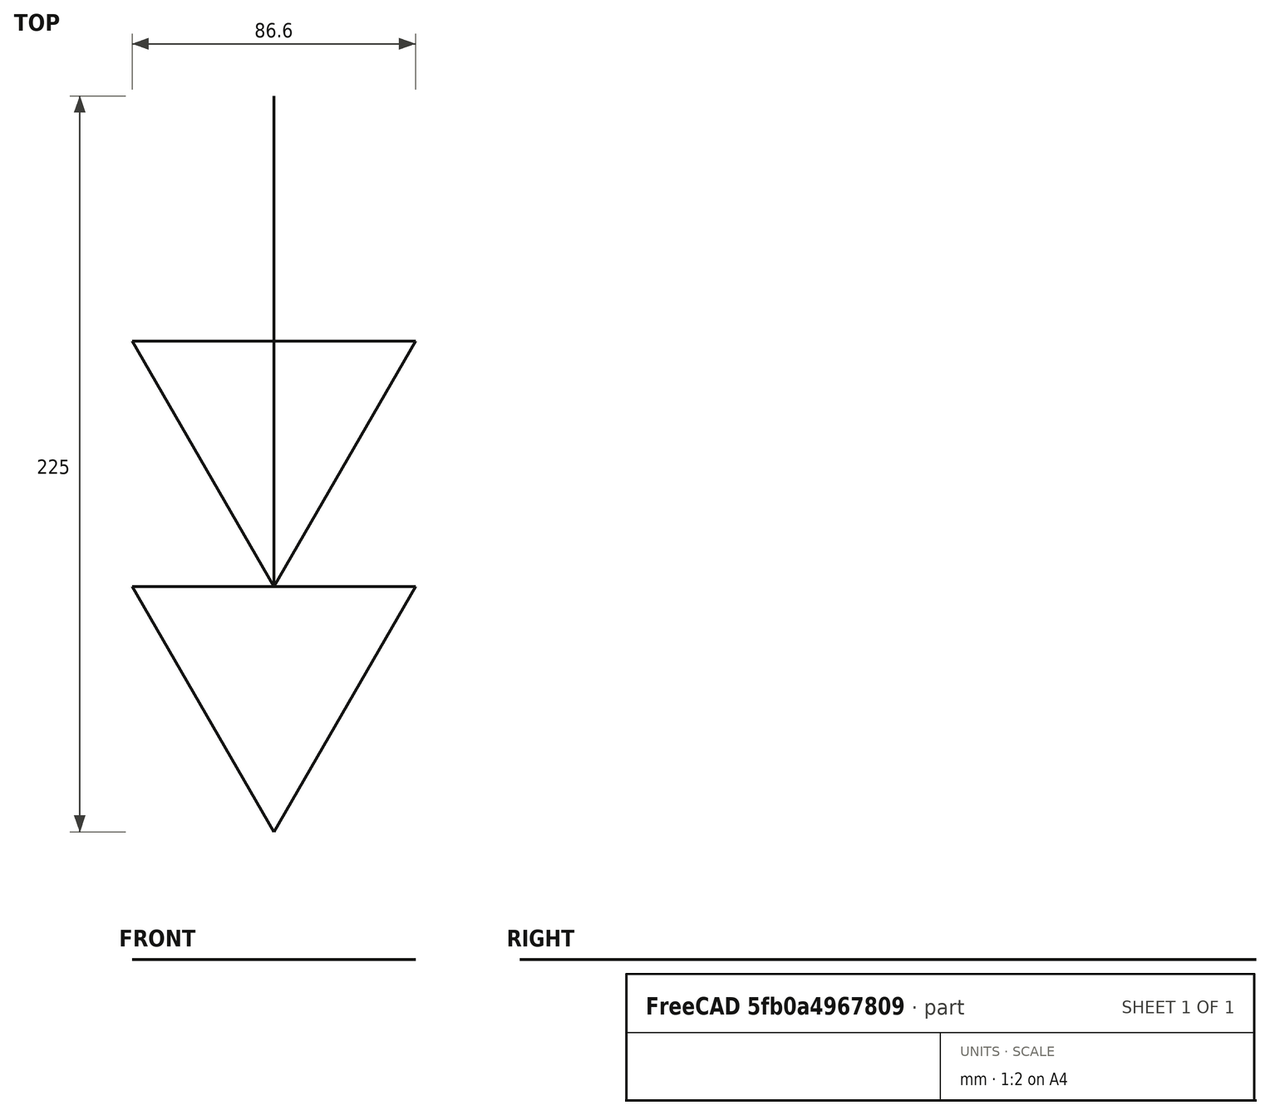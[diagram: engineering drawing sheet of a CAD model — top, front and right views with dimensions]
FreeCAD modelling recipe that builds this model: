
FCSTD DOCUMENT  (FreeCAD 1.1R20260325 (Git shallow))
Label: Tomada_Alta_2modulo_110v_com_simbologia
License: All rights reserved
LicenseURL: http://en.wikipedia.org/wiki/All_rights_reserved
objects: Part::FeaturePython×1, Part::Feature×1, App::DocumentObjectGroup×1
note: 2 computed .brp shape members not serialized (recipe doc carries the construction recipe); baked Part::Feature solids carry a one-line shape summary decoded from their .brp

FEATURE [Part::FeaturePython] Component  label="Tomada_2modulos_110v_alta"  # Arch/BIM 0 (typed FeaturePython)
  HorizontalArea = 0
  IfcData = attributes={"GlobalId": {"name": "GlobalId", "type": "IfcGloballyUniqueId", "is_enum": false, "enum_values": []}, "Description": {"... (+538 chars omitted),+1 more (map truncated)
  IfcType = 0
  MoveBase = false
  MoveWithHost = false
  PerimeterLength = 0
  Placement = pos=(0,0,2250) rot=(0,0,1;0rad)
  PredefinedType = 0
  VerticalArea = 0
FEATURE [Part::Feature] Compound002002002004005002002003003002003005002002005002002002002002002003  label="Simbologia_Tomada_alta"
  Placement = pos=(-87.5918,335.685,2241.87) rot=(0,0,1;0rad)
  shape: bbox 86.6 x 225 x 2e-07 mm, 2 faces, 0 solids (baked)
FEATURE [App::DocumentObjectGroup] Group  label="Tomada_2modulos_Alta"
  Group = -> [Component,Compound002002002004005002002003003002003005002002005002002002002002002003]
